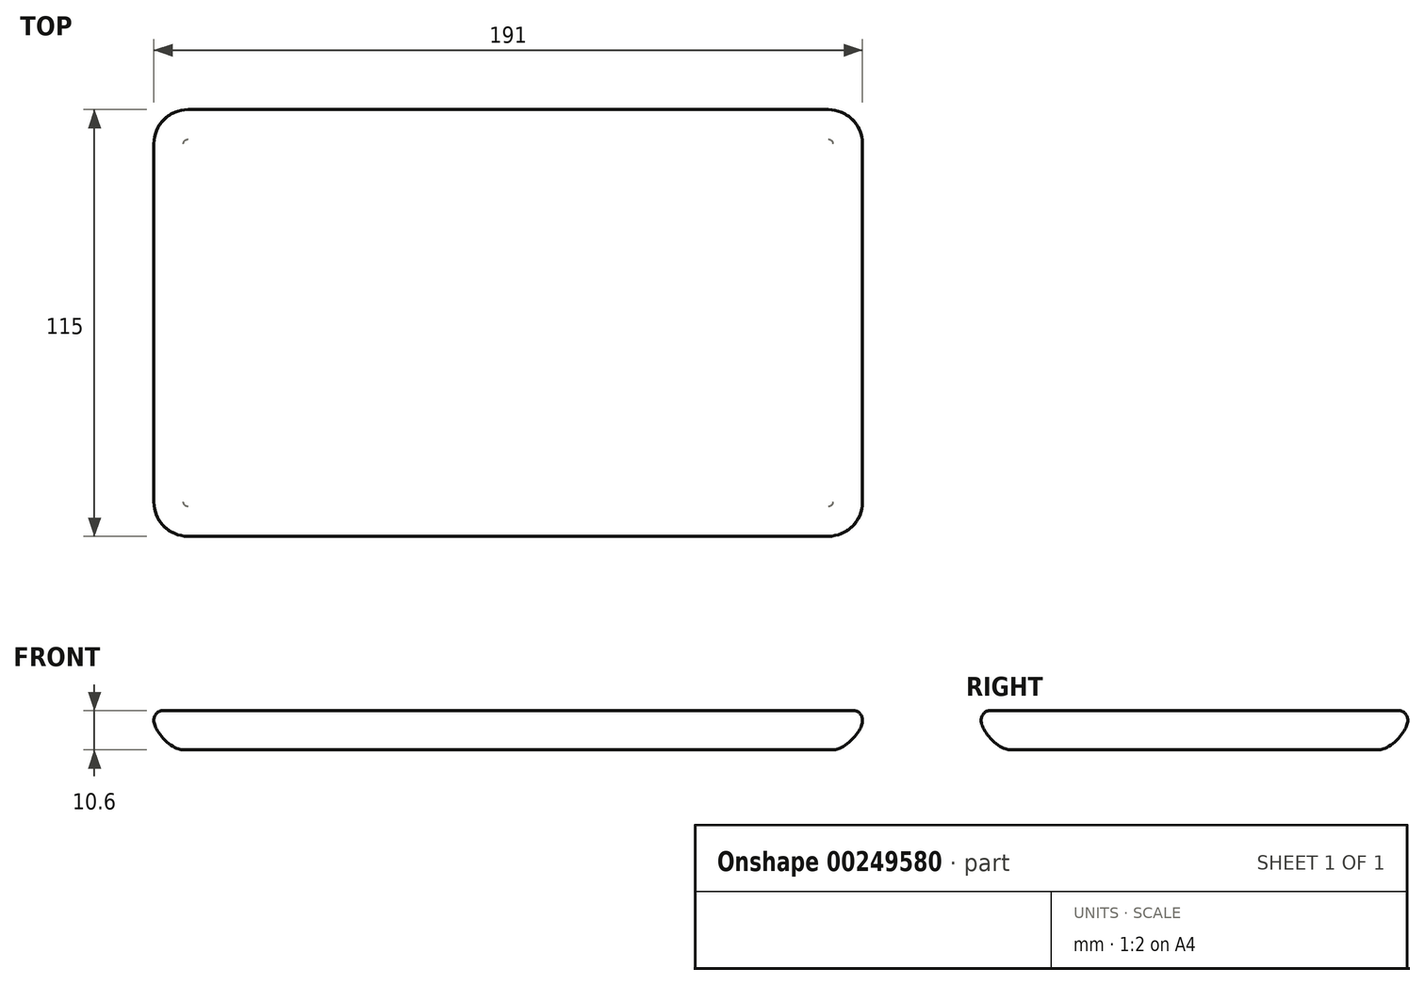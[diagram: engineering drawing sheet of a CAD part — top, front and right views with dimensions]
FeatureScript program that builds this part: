
annotation { "Feature Type Name" : "Feature", "Feature Type Description" : "" }
export const myFeature = defineFeature(function(context is Context, id is Id, definition is map)
    precondition{}
    {
        {
            assignVariable(context, id + "F0", {"name" : "DeviceDepth", "anyValue" : 10.6});
        }
        {
            var Q0;
            Q0=qCreatedBy(makeId("Top.planeOp"),FACE);
            var sketch = newSketch(context, id + "F1", { "sketchPlane" : qUnion([Q0])});
            skLineSegment(sketch, "E0.bottom", {"start": v(95.5, 57.5) * mm, "end": v(-95.5, 57.5) * mm});
            skLineSegment(sketch, "E0.top", {"start": v(95.5, -57.5) * mm, "end": v(-95.5, -57.5) * mm});
            skLineSegment(sketch, "E0.left", {"start": v(95.5, 57.5) * mm, "end": v(95.5, -57.5) * mm});
            skLineSegment(sketch, "E0.right", {"start": v(-95.5, 57.5) * mm, "end": v(-95.5, -57.5) * mm});
            skPoint(sketch, "E0.middle", {"position": v(0, 0) * mm});
            skSolve(sketch);
        }
        {
            var Q0;
            Q0=makeQuery(id+"F1.imprint","IMPRINT",FACE,{"disambiguationData":[TD([[makeQuery(id+"F1.imprint","IMPRINT",EDGE,{"derivedFrom":sQuery(id+"F1.wireOp",EDGE,"E0.bottom")}),1.0]])]});
            extrude(context, id + "F2", {"entities" : qUnion([Q0]), "depth" : (getVariable(context, 'DeviceDepth')) * mm});
        }
        {
            var Q0;
            Q0=makeQuery(id+"F2.opExtrude","SWEPT_EDGE",EDGE,{"disambiguationData":[OSD([sQuery(id+"F1.wireOp",EDGE,"E0.top"),sQuery(id+"F1.wireOp",EDGE,"E0.right")])]});
            var Q1;
            Q1=makeQuery(id+"F2.opExtrude","SWEPT_EDGE",EDGE,{"disambiguationData":[OSD([sQuery(id+"F1.wireOp",EDGE,"E0.bottom"),sQuery(id+"F1.wireOp",EDGE,"E0.right")])]});
            var Q2;
            Q2=makeQuery(id+"F2.opExtrude","SWEPT_EDGE",EDGE,{"disambiguationData":[OSD([sQuery(id+"F1.wireOp",EDGE,"E0.bottom"),sQuery(id+"F1.wireOp",EDGE,"E0.left")])]});
            var Q3;
            Q3=makeQuery(id+"F2.opExtrude","SWEPT_EDGE",EDGE,{"disambiguationData":[OSD([sQuery(id+"F1.wireOp",EDGE,"E0.top"),sQuery(id+"F1.wireOp",EDGE,"E0.left")])]});
            fillet(context, id + "F3", {"entities" : qUnion([Q0, Q1, Q2, Q3]), "radius" : 9.2 * mm, "tangentPropagation" : true, "allowEdgeOverflow" : false});
        }
        {
            var Q0;
            Q0=makeQuery(id+"F2.opExtrude","CAP_EDGE",EDGE,{"disambiguationData":[OSD([sQuery(id+"F1.wireOp",EDGE,"E0.top")])],"isStart":true});
            var Q1;
            Q1=makeQuery(id+"F2.opExtrude","CAP_EDGE",EDGE,{"disambiguationData":[OSD([sQuery(id+"F1.wireOp",EDGE,"E0.right")])],"isStart":true});
            var Q2;
            Q2=makeQuery(id+"F2.opExtrude","CAP_EDGE",EDGE,{"disambiguationData":[OSD([sQuery(id+"F1.wireOp",EDGE,"E0.bottom")])],"isStart":true});
            var Q3;
            Q3=makeQuery(id+"F2.opExtrude","CAP_EDGE",EDGE,{"disambiguationData":[OSD([sQuery(id+"F1.wireOp",EDGE,"E0.left")])],"isStart":true});
            fillet(context, id + "F4", {"entities" : qUnion([Q0, Q1, Q2, Q3]), "radius" : 8 * mm, "tangentPropagation" : true, "rho" : 0.3, "crossSection" : FilletCrossSection.CONIC, "allowEdgeOverflow" : false});
        }
        {
            var Q0;
            Q0=makeQuery(id+"F2.opExtrude","CAP_EDGE",EDGE,{"disambiguationData":[OSD([sQuery(id+"F1.wireOp",EDGE,"E0.left")])],"isStart":false});
            fillet(context, id + "F5", {"entities" : qUnion([Q0]), "radius" : 2.5 * mm, "tangentPropagation" : true, "allowEdgeOverflow" : false});
        }
    });
